# Revit family: S-756
name_source: partatom
category: Plumbing Fixtures
revit_build: Autodesk Revit 2015 (Build: 20140606_1530(x64)
units: mm (PartAtom-declared; Revit-internal decimal feet)

## types (6) — shared parameters
B = 52 mm
Description = CHANNEL GRID, BUBBLE, FOR CHANNELS WIDTH 50
Grid = INOX AISI304
Manufacturer = Jimten
Material = INOX AISI304
Model = S-756
Type Comments = COMPATIBLE WITH VISIBLE OR THIN FRAMES
URL = http://www.jimten.com

## per-type parameters (varying)
| type | A | N_MatrizHuecos | Reference | Size |
| 50x350mm_BUBBLE | 340 mm  [stored 1.11549 ft] | 3 | 13539 | 350mm x 50mm |
| 50x550mm_BUBBLE | 540 mm  [stored 1.77165 ft] | 5 | 13559 | 550mm x 50mm |
| 50x650mm_BUBBLE | 640 mm  [stored 2.09974 ft] | 6 | 13569 | 650mm x 50mm |
| 50x750mm_BUBBLE | 740 mm  [stored 2.42782 ft] | 7 | 13579 | 750mm x 50mm |
| 50x850mm_BUBBLE | 840 mm  [stored 2.75591 ft] | 8 | 13589 | 850mm x 50mm |
| 50x950mm_BUBBLE | 940 mm  [stored 3.08399 ft] | 9 | 13599 | 950mm x 50mm |

note: [stored X ft] marks values corroborated as IEEE doubles in the binary element streams (Revit-internal decimal feet)

## geometry (parser evidence)
native form markers: Blend x3, Sweep x1
no freeform markers — native parametric forms only
